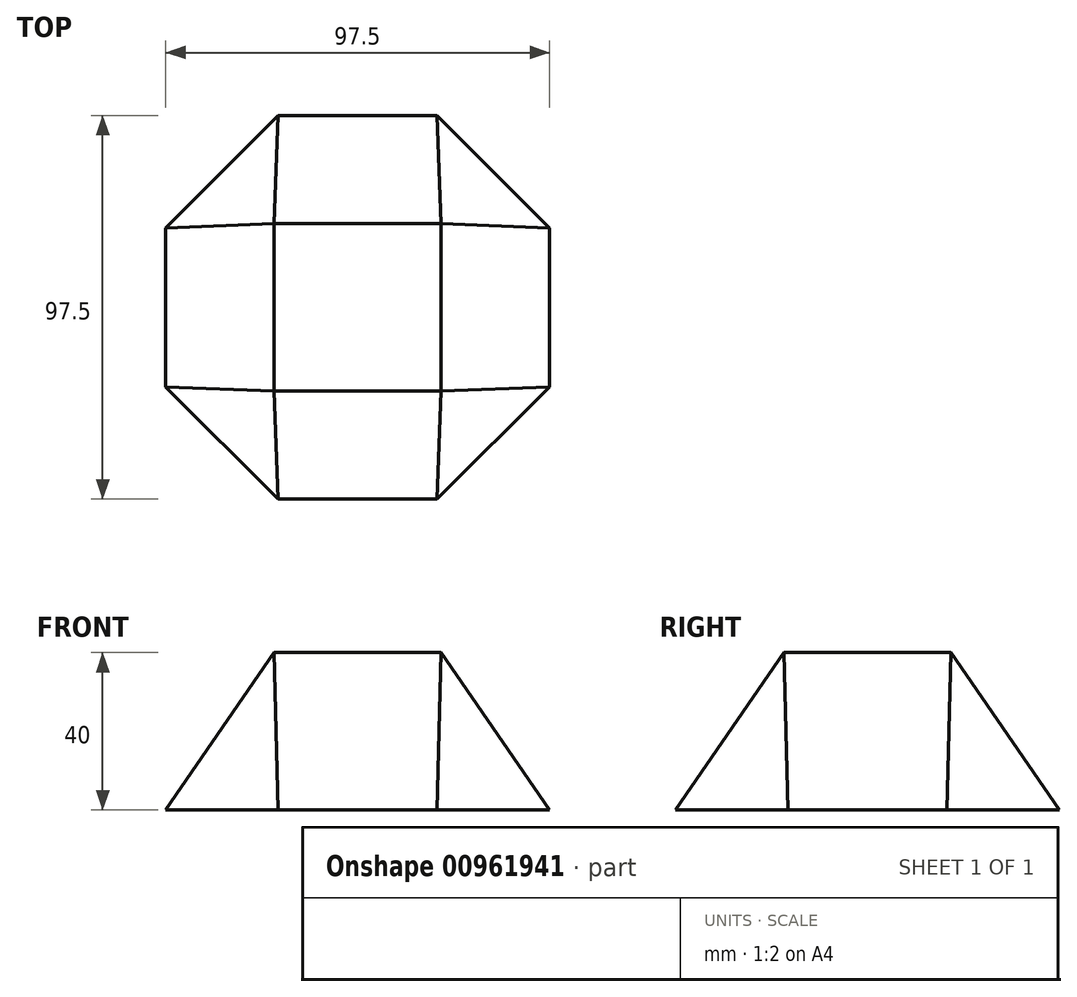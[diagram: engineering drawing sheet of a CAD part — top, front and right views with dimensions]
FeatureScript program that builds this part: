
annotation { "Feature Type Name" : "Feature", "Feature Type Description" : "" }
export const myFeature = defineFeature(function(context is Context, id is Id, definition is map)
    precondition{}
    {
        {
            var Q0;
            Q0=qCreatedBy(makeId("Top.planeOp"),FACE);
            var sketch = newSketch(context, id + "F0", { "sketchPlane" : qUnion([Q0])});
            skCircle(sketch, "E0", {"center": v(0, 0) * mm, "radius": 48.75 * mm});
            skCircle(sketch, "E1.cCircle", {"center": v(0, 0) * mm, "radius": 48.75 * mm, "construction": true});
            skLineSegment(sketch, "E1.0", {"start": v(-48.75, -20.2) * mm, "end": v(-48.75, 20.2) * mm});
            skLineSegment(sketch, "E1.1", {"start": v(-48.75, 20.2) * mm, "end": v(-20.2, 48.75) * mm});
            skLineSegment(sketch, "E1.2", {"start": v(-20.2, 48.75) * mm, "end": v(20.2, 48.75) * mm});
            skLineSegment(sketch, "E1.3", {"start": v(20.2, 48.75) * mm, "end": v(48.75, 20.2) * mm});
            skLineSegment(sketch, "E1.4", {"start": v(48.75, 20.2) * mm, "end": v(48.75, -20.2) * mm});
            skLineSegment(sketch, "E1.5", {"start": v(48.75, -20.2) * mm, "end": v(20.2, -48.75) * mm});
            skLineSegment(sketch, "E1.6", {"start": v(20.2, -48.75) * mm, "end": v(-20.2, -48.75) * mm});
            skLineSegment(sketch, "E1.7", {"start": v(-20.2, -48.75) * mm, "end": v(-48.75, -20.2) * mm});
            skPoint(sketch, "E1.0.midPoint", {"position": v(-48.75, 0) * mm});
            skSolve(sketch);
        }
        {
            var Q0;
            Q0 = qSketchRegion(id + "F0", true);
            extrude(context, id + "F1", {"entities" : qUnion([Q0]), "depth" : 2 * mm, "offsetDistance" : 25 * mm});
        }
        {
            var Q0;
            Q0=makeQuery(id+"F1.opExtrude","CAP_FACE",FACE,{"disambiguationData":[OSD([sQuery(id+"F0.wireOp",EDGE,"E1.0"),sQuery(id+"F0.wireOp",EDGE,"E1.1"),sQuery(id+"F0.wireOp",EDGE,"E1.2"),sQuery(id+"F0.wireOp",EDGE,"E1.3"),sQuery(id+"F0.wireOp",EDGE,"E1.4"),sQuery(id+"F0.wireOp",EDGE,"E1.5"),sQuery(id+"F0.wireOp",EDGE,"E1.6"),sQuery(id+"F0.wireOp",EDGE,"E1.7")])],"isStart":false});
            cPlane(context, id + "F2", {"entities" : qUnion([Q0]), "cplaneType" : CPlaneType.OFFSET, "offset" : 40 * mm, "width" : 150 * mm, "height" : 150 * mm});
        }
        {
            var Q0;
            Q0=qCreatedBy(id+"F2.planeOp",FACE);
            var sketch = newSketch(context, id + "F3", { "sketchPlane" : qUnion([Q0])});
            skLineSegment(sketch, "E2.0", {"start": v(-30, -12.43) * mm, "end": v(-30, 12.43) * mm});
            skLineSegment(sketch, "E2.1", {"start": v(-30, 12.43) * mm, "end": v(-12.43, 30) * mm});
            skLineSegment(sketch, "E2.2", {"start": v(-12.43, 30) * mm, "end": v(12.43, 30) * mm});
            skLineSegment(sketch, "E2.3", {"start": v(12.43, 30) * mm, "end": v(30, 12.43) * mm});
            skLineSegment(sketch, "E2.4", {"start": v(30, 12.43) * mm, "end": v(30, -12.43) * mm});
            skLineSegment(sketch, "E2.5", {"start": v(30, -12.43) * mm, "end": v(12.43, -30) * mm});
            skLineSegment(sketch, "E2.6", {"start": v(12.43, -30) * mm, "end": v(-12.43, -30) * mm});
            skLineSegment(sketch, "E2.7", {"start": v(-12.43, -30) * mm, "end": v(-30, -12.43) * mm});
            skPoint(sketch, "E2.0.midPoint", {"position": v(-30, 0) * mm});
            skSolve(sketch);
        }
        {
            var Q0;
            Q0=makeQuery(id+"F1.opExtrude","CAP_FACE",FACE,{"disambiguationData":[OSD([sQuery(id+"F0.wireOp",EDGE,"E1.0"),sQuery(id+"F0.wireOp",EDGE,"E1.1"),sQuery(id+"F0.wireOp",EDGE,"E1.2"),sQuery(id+"F0.wireOp",EDGE,"E1.3"),sQuery(id+"F0.wireOp",EDGE,"E1.4"),sQuery(id+"F0.wireOp",EDGE,"E1.5"),sQuery(id+"F0.wireOp",EDGE,"E1.6"),sQuery(id+"F0.wireOp",EDGE,"E1.7")])],"isStart":false});
            var sketch = newSketch(context, id + "F4", { "sketchPlane" : qUnion([Q0])});
            skCircle(sketch, "E3.cCircle", {"center": v(0, 0) * mm, "radius": 48.75 * mm, "construction": true});
            skLineSegment(sketch, "E3.0", {"start": v(-48.75, -20.2) * mm, "end": v(-48.75, 20.2) * mm});
            skLineSegment(sketch, "E3.1", {"start": v(-48.75, 20.2) * mm, "end": v(-20.2, 48.75) * mm});
            skLineSegment(sketch, "E3.2", {"start": v(-20.2, 48.75) * mm, "end": v(20.2, 48.75) * mm});
            skLineSegment(sketch, "E3.3", {"start": v(20.2, 48.75) * mm, "end": v(48.75, 20.2) * mm});
            skLineSegment(sketch, "E3.4", {"start": v(48.75, 20.2) * mm, "end": v(48.75, -20.2) * mm});
            skLineSegment(sketch, "E3.5", {"start": v(48.75, -20.2) * mm, "end": v(20.2, -48.75) * mm});
            skLineSegment(sketch, "E3.6", {"start": v(20.2, -48.75) * mm, "end": v(-20.2, -48.75) * mm});
            skLineSegment(sketch, "E3.7", {"start": v(-20.2, -48.75) * mm, "end": v(-48.75, -20.2) * mm});
            skPoint(sketch, "E3.0.midPoint", {"position": v(-48.75, 0) * mm});
            skSolve(sketch);
        }
        {
            var Q1;
            Q1 = qSketchRegion(id + "F4", true);
            var Q2;
            Q2 = qSketchRegion(id + "F3", true);
            loft(context, id + "F5", {"operationType" : NewBodyOperationType.ADD, "sheetProfilesArray" : [{ "sheetProfileEntities" : qUnion([Q1]) }, { "sheetProfileEntities" : qUnion([Q2]) }]});
        }
        {
            var Q0;
            Q0=makeQuery(id+"F1.opExtrude","CAP_FACE",FACE,{"disambiguationData":[OSD([sQuery(id+"F0.wireOp",EDGE,"E1.0"),sQuery(id+"F0.wireOp",EDGE,"E1.1"),sQuery(id+"F0.wireOp",EDGE,"E1.2"),sQuery(id+"F0.wireOp",EDGE,"E1.3"),sQuery(id+"F0.wireOp",EDGE,"E1.4"),sQuery(id+"F0.wireOp",EDGE,"E1.5"),sQuery(id+"F0.wireOp",EDGE,"E1.6"),sQuery(id+"F0.wireOp",EDGE,"E1.7")])],"isStart":true});
            cPlane(context, id + "F6", {"entities" : qUnion([Q0]), "cplaneType" : CPlaneType.OFFSET, "offset" : 2 * mm, "oppositeDirection" : true, "width" : 150 * mm, "height" : 150 * mm});
        }
        {
            var Q0;
            Q0=qCreatedBy(id+"F6.planeOp",FACE);
            var sketch = newSketch(context, id + "F7", { "sketchPlane" : qUnion([Q0])});
            skLineSegment(sketch, "E4.bottom", {"start": v(-48.75, -48.75) * mm, "end": v(48.75, -48.75) * mm});
            skLineSegment(sketch, "E4.top", {"start": v(-48.75, 48.75) * mm, "end": v(48.75, 48.75) * mm});
            skLineSegment(sketch, "E4.left", {"start": v(-48.75, -48.75) * mm, "end": v(-48.75, 48.75) * mm});
            skLineSegment(sketch, "E4.right", {"start": v(48.75, -48.75) * mm, "end": v(48.75, 48.75) * mm});
            skPoint(sketch, "E4.middle", {"position": v(0, 0) * mm});
            skSolve(sketch);
        }
        {
            var Q0;
            Q0=makeQuery(id+"F5.opLoft","CAP_FACE",FACE,{"disambiguationData":[OSD([makeQuery(id+"F3.imprint","IMPRINT",FACE,{"disambiguationData":[TD([[makeQuery(id+"F3.imprint","IMPRINT",EDGE,{"derivedFrom":sQuery(id+"F3.wireOp",EDGE,"E2.0")}),-1.0]])]})])],"isStart":true});
            var sketch = newSketch(context, id + "F8", { "sketchPlane" : qUnion([Q0])});
            skLineSegment(sketch, "E5.bottom", {"start": v(21.21, 21.21) * mm, "end": v(-21.21, 21.21) * mm});
            skLineSegment(sketch, "E5.top", {"start": v(21.21, -21.21) * mm, "end": v(-21.21, -21.21) * mm});
            skLineSegment(sketch, "E5.left", {"start": v(21.21, 21.21) * mm, "end": v(21.21, -21.21) * mm});
            skLineSegment(sketch, "E5.right", {"start": v(-21.21, 21.21) * mm, "end": v(-21.21, -21.21) * mm});
            skPoint(sketch, "E5.middle", {"position": v(0, 0) * mm});
            skSolve(sketch);
        }
        {
            var Q1;
            Q1=makeQuery(id+"F7.imprint","IMPRINT",FACE,{"disambiguationData":[TD([[makeQuery(id+"F7.imprint","IMPRINT",EDGE,{"derivedFrom":sQuery(id+"F7.wireOp",EDGE,"E4.bottom")}),1.0]])]});
            var Q2;
            Q2=makeQuery(id+"F8.imprint","IMPRINT",FACE,{"disambiguationData":[TD([[makeQuery(id+"F8.imprint","IMPRINT",EDGE,{"derivedFrom":sQuery(id+"F8.wireOp",EDGE,"E5.bottom")}),1.0]])]});
            loft(context, id + "F9", {"operationType" : NewBodyOperationType.INTERSECT, "sheetProfilesArray" : [{ "sheetProfileEntities" : qUnion([Q1]) }, { "sheetProfileEntities" : qUnion([Q2]) }]});
        }
    });
